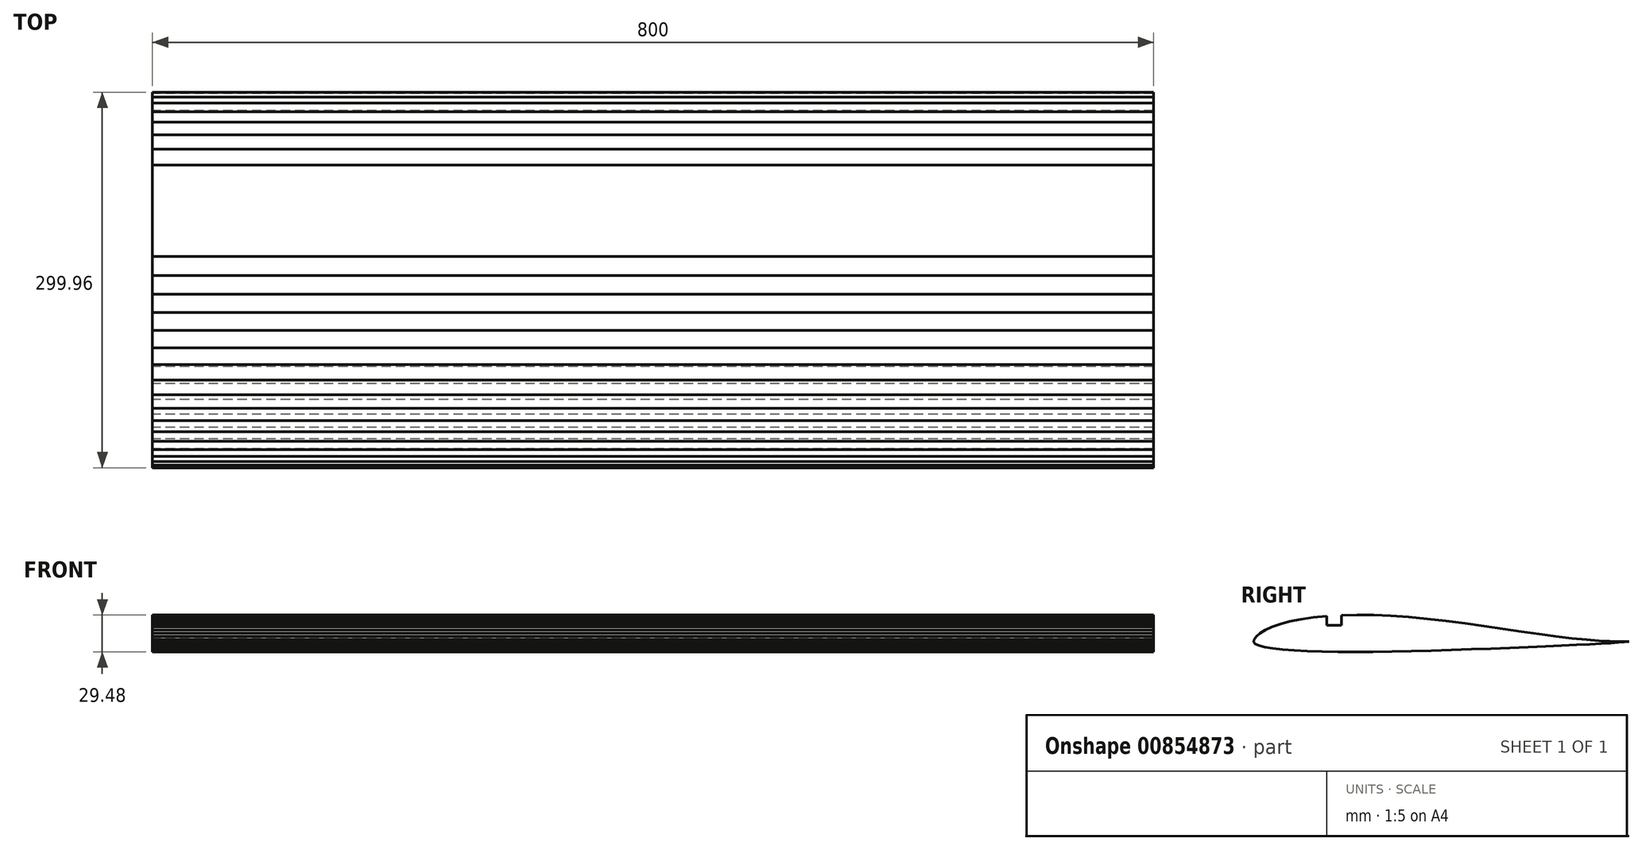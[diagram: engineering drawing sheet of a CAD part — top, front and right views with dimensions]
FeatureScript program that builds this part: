
annotation { "Feature Type Name" : "Feature", "Feature Type Description" : "" }
export const myFeature = defineFeature(function(context is Context, id is Id, definition is map)
    precondition{}
    {
        {
            var Q0;
            Q0=qCreatedBy(makeId("Right.planeOp"),FACE);
            var sketch = newSketch(context, id + "F0", { "sketchPlane" : qUnion([Q0])});
            skLineSegment(sketch, "E0", {"start": v(149.98, -6.6) * mm, "end": v(149, -6.6) * mm});
            skLineSegment(sketch, "E1", {"start": v(149, -6.6) * mm, "end": v(146.1, -6.58) * mm});
            skLineSegment(sketch, "E2", {"start": v(146.1, -6.58) * mm, "end": v(141.28, -6.49) * mm});
            skLineSegment(sketch, "E3", {"start": v(141.28, -6.49) * mm, "end": v(134.59, -6.27) * mm});
            skLineSegment(sketch, "E4", {"start": v(134.59, -6.27) * mm, "end": v(126.1, -5.83) * mm});
            skLineSegment(sketch, "E5", {"start": v(126.1, -5.83) * mm, "end": v(115.98, -5.05) * mm});
            skLineSegment(sketch, "E6", {"start": v(115.98, -5.05) * mm, "end": v(104.46, -3.89) * mm});
            skLineSegment(sketch, "E7", {"start": v(104.46, -3.89) * mm, "end": v(91.8, -2.38) * mm});
            skLineSegment(sketch, "E8", {"start": v(91.8, -2.38) * mm, "end": v(78.2, -0.57) * mm});
            skLineSegment(sketch, "E9", {"start": v(78.2, -0.57) * mm, "end": v(63.9, 1.47) * mm});
            skLineSegment(sketch, "E10", {"start": v(63.9, 1.47) * mm, "end": v(49.1, 3.66) * mm});
            skLineSegment(sketch, "E11", {"start": v(49.1, 3.66) * mm, "end": v(34.04, 5.9) * mm});
            skLineSegment(sketch, "E12", {"start": v(34.04, 5.9) * mm, "end": v(18.87, 8.03) * mm});
            skLineSegment(sketch, "E13", {"start": v(18.87, 8.03) * mm, "end": v(3.72, 9.99) * mm});
            skLineSegment(sketch, "E14", {"start": v(3.72, 9.99) * mm, "end": v(-11.27, 11.68) * mm});
            skLineSegment(sketch, "E15", {"start": v(-11.27, 11.68) * mm, "end": v(-25.98, 13.04) * mm});
            skLineSegment(sketch, "E16", {"start": v(-25.98, 13.04) * mm, "end": v(-40.3, 14.02) * mm});
            skLineSegment(sketch, "E17", {"start": v(-40.3, 14.02) * mm, "end": v(-54.12, 14.6) * mm});
            skLineSegment(sketch, "E18", {"start": v(-54.12, 14.6) * mm, "end": v(-67.34, 14.74) * mm});
            skLineSegment(sketch, "E19", {"start": v(-67.34, 14.74) * mm, "end": v(-79.87, 14.47) * mm});
            skLineSegment(sketch, "E20", {"start": v(-79.87, 14.47) * mm, "end": v(-91.6, 13.8) * mm});
            skLineSegment(sketch, "E21", {"start": v(-91.6, 13.8) * mm, "end": v(-102.44, 12.74) * mm});
            skLineSegment(sketch, "E22", {"start": v(-102.44, 12.74) * mm, "end": v(-112.3, 11.3) * mm});
            skLineSegment(sketch, "E23", {"start": v(-112.3, 11.3) * mm, "end": v(-121.11, 9.53) * mm});
            skLineSegment(sketch, "E24", {"start": v(-121.11, 9.53) * mm, "end": v(-128.8, 7.47) * mm});
            skLineSegment(sketch, "E25", {"start": v(-128.8, 7.47) * mm, "end": v(-135.36, 5.15) * mm});
            skLineSegment(sketch, "E26", {"start": v(-135.36, 5.15) * mm, "end": v(-140.72, 2.65) * mm});
            skLineSegment(sketch, "E27", {"start": v(-140.72, 2.65) * mm, "end": v(-144.87, 0.04) * mm});
            skLineSegment(sketch, "E28", {"start": v(-144.87, 0.04) * mm, "end": v(-147.8, -2.55) * mm});
            skLineSegment(sketch, "E29", {"start": v(-147.8, -2.55) * mm, "end": v(-149.52, -5) * mm});
            skLineSegment(sketch, "E30", {"start": v(-149.52, -5) * mm, "end": v(-149.98, -7.02) * mm});
            skLineSegment(sketch, "E31", {"start": v(-149.98, -7.02) * mm, "end": v(-148.75, -8.55) * mm});
            skLineSegment(sketch, "E32", {"start": v(-148.75, -8.55) * mm, "end": v(-145.65, -9.85) * mm});
            skLineSegment(sketch, "E33", {"start": v(-145.65, -9.85) * mm, "end": v(-140.94, -11.01) * mm});
            skLineSegment(sketch, "E34", {"start": v(-140.94, -11.01) * mm, "end": v(-134.65, -12) * mm});
            skLineSegment(sketch, "E35", {"start": v(-134.65, -12) * mm, "end": v(-126.87, -12.84) * mm});
            skLineSegment(sketch, "E36", {"start": v(-126.87, -12.84) * mm, "end": v(-117.67, -13.52) * mm});
            skLineSegment(sketch, "E37", {"start": v(-117.67, -13.52) * mm, "end": v(-107.15, -14.04) * mm});
            skLineSegment(sketch, "E38", {"start": v(-107.15, -14.04) * mm, "end": v(-95.44, -14.42) * mm});
            skLineSegment(sketch, "E39", {"start": v(-95.44, -14.42) * mm, "end": v(-82.68, -14.66) * mm});
            skLineSegment(sketch, "E40", {"start": v(-82.68, -14.66) * mm, "end": v(-69, -14.74) * mm});
            skLineSegment(sketch, "E41", {"start": v(-69, -14.74) * mm, "end": v(-54.54, -14.67) * mm});
            skLineSegment(sketch, "E42", {"start": v(-54.54, -14.67) * mm, "end": v(-39.43, -14.47) * mm});
            skLineSegment(sketch, "E43", {"start": v(-39.43, -14.47) * mm, "end": v(-23.86, -14.15) * mm});
            skLineSegment(sketch, "E44", {"start": v(-23.86, -14.15) * mm, "end": v(-7.99, -13.74) * mm});
            skLineSegment(sketch, "E45", {"start": v(-7.99, -13.74) * mm, "end": v(8, -13.25) * mm});
            skLineSegment(sketch, "E46", {"start": v(8, -13.25) * mm, "end": v(23.93, -12.71) * mm});
            skLineSegment(sketch, "E47", {"start": v(23.93, -12.71) * mm, "end": v(39.6, -12.14) * mm});
            skLineSegment(sketch, "E48", {"start": v(39.6, -12.14) * mm, "end": v(54.85, -11.53) * mm});
            skLineSegment(sketch, "E49", {"start": v(54.85, -11.53) * mm, "end": v(69.5, -10.93) * mm});
            skLineSegment(sketch, "E50", {"start": v(69.5, -10.93) * mm, "end": v(83.35, -10.33) * mm});
            skLineSegment(sketch, "E51", {"start": v(83.35, -10.33) * mm, "end": v(96.26, -9.74) * mm});
            skLineSegment(sketch, "E52", {"start": v(96.26, -9.74) * mm, "end": v(108.07, -9.2) * mm});
            skLineSegment(sketch, "E53", {"start": v(108.07, -9.2) * mm, "end": v(118.62, -8.67) * mm});
            skLineSegment(sketch, "E54", {"start": v(118.62, -8.67) * mm, "end": v(127.79, -8.18) * mm});
            skLineSegment(sketch, "E55", {"start": v(127.79, -8.18) * mm, "end": v(135.47, -7.7) * mm});
            skLineSegment(sketch, "E56", {"start": v(135.47, -7.7) * mm, "end": v(141.61, -7.23) * mm});
            skLineSegment(sketch, "E57", {"start": v(141.61, -7.23) * mm, "end": v(146.17, -6.86) * mm});
            skLineSegment(sketch, "E58", {"start": v(146.17, -6.86) * mm, "end": v(149.01, -6.65) * mm});
            skLineSegment(sketch, "E59", {"start": v(149.01, -6.65) * mm, "end": v(149.98, -6.6) * mm});
            skSolve(sketch);
        }
        {
            var Q0;
            Q0=makeQuery(id+"F0.imprint","IMPRINT",FACE,{"disambiguationData":[TD([[makeQuery(id+"F0.imprint","IMPRINT",EDGE,{"derivedFrom":sQuery(id+"F0.wireOp",EDGE,"E0")}),1.0]])]});
            extrude(context, id + "F1", {"entities" : qUnion([Q0]), "depth" : 800 * mm, "offsetDistance" : 25 * mm});
        }
        {
            var Q0;
            Q0=makeQuery(id+"F1.opExtrude","CAP_FACE",FACE,{"disambiguationData":[OSD([sQuery(id+"F0.wireOp",EDGE,"E0"),sQuery(id+"F0.wireOp",EDGE,"E1"),sQuery(id+"F0.wireOp",EDGE,"E2"),sQuery(id+"F0.wireOp",EDGE,"E3"),sQuery(id+"F0.wireOp",EDGE,"E4"),sQuery(id+"F0.wireOp",EDGE,"E5"),sQuery(id+"F0.wireOp",EDGE,"E6"),sQuery(id+"F0.wireOp",EDGE,"E7"),sQuery(id+"F0.wireOp",EDGE,"E8"),sQuery(id+"F0.wireOp",EDGE,"E9"),sQuery(id+"F0.wireOp",EDGE,"E10"),sQuery(id+"F0.wireOp",EDGE,"E11"),sQuery(id+"F0.wireOp",EDGE,"E12"),sQuery(id+"F0.wireOp",EDGE,"E13"),sQuery(id+"F0.wireOp",EDGE,"E14"),sQuery(id+"F0.wireOp",EDGE,"E15"),sQuery(id+"F0.wireOp",EDGE,"E16"),sQuery(id+"F0.wireOp",EDGE,"E17"),sQuery(id+"F0.wireOp",EDGE,"E18"),sQuery(id+"F0.wireOp",EDGE,"E19"),sQuery(id+"F0.wireOp",EDGE,"E20"),sQuery(id+"F0.wireOp",EDGE,"E21"),sQuery(id+"F0.wireOp",EDGE,"E22"),sQuery(id+"F0.wireOp",EDGE,"E23"),sQuery(id+"F0.wireOp",EDGE,"E24"),sQuery(id+"F0.wireOp",EDGE,"E25"),sQuery(id+"F0.wireOp",EDGE,"E26"),sQuery(id+"F0.wireOp",EDGE,"E27"),sQuery(id+"F0.wireOp",EDGE,"E28"),sQuery(id+"F0.wireOp",EDGE,"E29"),sQuery(id+"F0.wireOp",EDGE,"E30"),sQuery(id+"F0.wireOp",EDGE,"E31"),sQuery(id+"F0.wireOp",EDGE,"E32"),sQuery(id+"F0.wireOp",EDGE,"E33"),sQuery(id+"F0.wireOp",EDGE,"E34"),sQuery(id+"F0.wireOp",EDGE,"E35"),sQuery(id+"F0.wireOp",EDGE,"E36"),sQuery(id+"F0.wireOp",EDGE,"E37"),sQuery(id+"F0.wireOp",EDGE,"E38"),sQuery(id+"F0.wireOp",EDGE,"E39"),sQuery(id+"F0.wireOp",EDGE,"E40"),sQuery(id+"F0.wireOp",EDGE,"E41"),sQuery(id+"F0.wireOp",EDGE,"E42"),sQuery(id+"F0.wireOp",EDGE,"E43"),sQuery(id+"F0.wireOp",EDGE,"E44"),sQuery(id+"F0.wireOp",EDGE,"E45"),sQuery(id+"F0.wireOp",EDGE,"E46"),sQuery(id+"F0.wireOp",EDGE,"E47"),sQuery(id+"F0.wireOp",EDGE,"E48"),sQuery(id+"F0.wireOp",EDGE,"E49"),sQuery(id+"F0.wireOp",EDGE,"E50"),sQuery(id+"F0.wireOp",EDGE,"E51"),sQuery(id+"F0.wireOp",EDGE,"E52"),sQuery(id+"F0.wireOp",EDGE,"E53"),sQuery(id+"F0.wireOp",EDGE,"E54"),sQuery(id+"F0.wireOp",EDGE,"E55"),sQuery(id+"F0.wireOp",EDGE,"E56"),sQuery(id+"F0.wireOp",EDGE,"E57"),sQuery(id+"F0.wireOp",EDGE,"E58"),sQuery(id+"F0.wireOp",EDGE,"E59")])],"isStart":false});
            var sketch = newSketch(context, id + "F2", { "sketchPlane" : qUnion([Q0])});
            skLineSegment(sketch, "E60.0.0", {"start": v(146.17, -6.86) * mm, "end": v(149.01, -6.65) * mm, "construction": true});
            skLineSegment(sketch, "E60.0.1", {"start": v(149.01, -6.65) * mm, "end": v(149.98, -6.6) * mm, "construction": true});
            skLineSegment(sketch, "E60.0.2", {"start": v(149.98, -6.6) * mm, "end": v(149, -6.6) * mm, "construction": true});
            skLineSegment(sketch, "E60.0.3", {"start": v(149, -6.6) * mm, "end": v(146.1, -6.58) * mm, "construction": true});
            skLineSegment(sketch, "E60.0.4", {"start": v(146.1, -6.58) * mm, "end": v(141.28, -6.49) * mm, "construction": true});
            skLineSegment(sketch, "E60.0.5", {"start": v(141.28, -6.49) * mm, "end": v(134.59, -6.27) * mm, "construction": true});
            skLineSegment(sketch, "E60.0.6", {"start": v(134.59, -6.27) * mm, "end": v(126.1, -5.83) * mm, "construction": true});
            skLineSegment(sketch, "E60.0.7", {"start": v(126.1, -5.83) * mm, "end": v(115.98, -5.05) * mm, "construction": true});
            skLineSegment(sketch, "E60.0.8", {"start": v(115.98, -5.05) * mm, "end": v(104.46, -3.89) * mm, "construction": true});
            skLineSegment(sketch, "E60.0.9", {"start": v(104.46, -3.89) * mm, "end": v(91.8, -2.38) * mm, "construction": true});
            skLineSegment(sketch, "E60.0.10", {"start": v(91.8, -2.38) * mm, "end": v(78.2, -0.57) * mm, "construction": true});
            skLineSegment(sketch, "E60.0.11", {"start": v(78.2, -0.57) * mm, "end": v(63.9, 1.47) * mm, "construction": true});
            skLineSegment(sketch, "E60.0.12", {"start": v(63.9, 1.47) * mm, "end": v(49.1, 3.66) * mm, "construction": true});
            skLineSegment(sketch, "E60.0.13", {"start": v(49.1, 3.66) * mm, "end": v(34.04, 5.9) * mm, "construction": true});
            skLineSegment(sketch, "E60.0.14", {"start": v(34.04, 5.9) * mm, "end": v(18.87, 8.03) * mm, "construction": true});
            skLineSegment(sketch, "E60.0.15", {"start": v(18.87, 8.03) * mm, "end": v(3.72, 10) * mm, "construction": true});
            skLineSegment(sketch, "E60.0.16", {"start": v(3.72, 9.99) * mm, "end": v(-11.27, 11.68) * mm, "construction": true});
            skLineSegment(sketch, "E60.0.17", {"start": v(-11.27, 11.68) * mm, "end": v(-25.98, 13.04) * mm, "construction": true});
            skLineSegment(sketch, "E60.0.18", {"start": v(-25.98, 13.04) * mm, "end": v(-40.3, 14.02) * mm, "construction": true});
            skLineSegment(sketch, "E60.0.19", {"start": v(-40.3, 14.02) * mm, "end": v(-54.12, 14.6) * mm, "construction": true});
            skLineSegment(sketch, "E60.0.20", {"start": v(-54.12, 14.6) * mm, "end": v(-67.34, 14.74) * mm, "construction": true});
            skLineSegment(sketch, "E60.0.21", {"start": v(-67.34, 14.74) * mm, "end": v(-79.87, 14.47) * mm, "construction": true});
            skLineSegment(sketch, "E60.0.22", {"start": v(-79.87, 14.47) * mm, "end": v(-91.6, 13.8) * mm, "construction": true});
            skLineSegment(sketch, "E60.0.23", {"start": v(-91.6, 13.8) * mm, "end": v(-102.44, 12.74) * mm, "construction": true});
            skLineSegment(sketch, "E60.0.24", {"start": v(-102.44, 12.74) * mm, "end": v(-112.3, 11.3) * mm, "construction": true});
            skLineSegment(sketch, "E60.0.25", {"start": v(-112.3, 11.3) * mm, "end": v(-121.11, 9.53) * mm, "construction": true});
            skLineSegment(sketch, "E60.0.26", {"start": v(-121.11, 9.53) * mm, "end": v(-128.8, 7.47) * mm, "construction": true});
            skLineSegment(sketch, "E60.0.27", {"start": v(-128.8, 7.47) * mm, "end": v(-135.36, 5.15) * mm, "construction": true});
            skLineSegment(sketch, "E60.0.28", {"start": v(-135.36, 5.15) * mm, "end": v(-140.72, 2.65) * mm, "construction": true});
            skLineSegment(sketch, "E60.0.29", {"start": v(-140.72, 2.65) * mm, "end": v(-144.87, 0.04) * mm, "construction": true});
            skLineSegment(sketch, "E60.0.30", {"start": v(-144.87, 0.04) * mm, "end": v(-147.8, -2.55) * mm, "construction": true});
            skLineSegment(sketch, "E60.0.31", {"start": v(-147.8, -2.55) * mm, "end": v(-149.52, -5) * mm, "construction": true});
            skLineSegment(sketch, "E60.0.32", {"start": v(-149.52, -5) * mm, "end": v(-149.98, -7.02) * mm, "construction": true});
            skLineSegment(sketch, "E60.0.33", {"start": v(-149.98, -7.02) * mm, "end": v(-148.75, -8.55) * mm, "construction": true});
            skLineSegment(sketch, "E60.0.34", {"start": v(-148.75, -8.55) * mm, "end": v(-145.65, -9.85) * mm, "construction": true});
            skLineSegment(sketch, "E60.0.35", {"start": v(-145.65, -9.85) * mm, "end": v(-140.94, -11.01) * mm, "construction": true});
            skLineSegment(sketch, "E60.0.36", {"start": v(-140.94, -11.01) * mm, "end": v(-134.65, -12) * mm, "construction": true});
            skLineSegment(sketch, "E60.0.37", {"start": v(-134.65, -12) * mm, "end": v(-126.87, -12.84) * mm, "construction": true});
            skLineSegment(sketch, "E60.0.38", {"start": v(-126.87, -12.84) * mm, "end": v(-117.67, -13.52) * mm, "construction": true});
            skLineSegment(sketch, "E60.0.39", {"start": v(-117.67, -13.52) * mm, "end": v(-107.15, -14.04) * mm, "construction": true});
            skLineSegment(sketch, "E60.0.40", {"start": v(-107.15, -14.04) * mm, "end": v(-95.44, -14.42) * mm, "construction": true});
            skLineSegment(sketch, "E60.0.41", {"start": v(-95.44, -14.42) * mm, "end": v(-82.68, -14.66) * mm, "construction": true});
            skLineSegment(sketch, "E60.0.42", {"start": v(-82.68, -14.66) * mm, "end": v(-69, -14.74) * mm, "construction": true});
            skLineSegment(sketch, "E60.0.43", {"start": v(-69, -14.74) * mm, "end": v(-54.54, -14.67) * mm, "construction": true});
            skLineSegment(sketch, "E60.0.44", {"start": v(-54.54, -14.67) * mm, "end": v(-39.43, -14.47) * mm, "construction": true});
            skLineSegment(sketch, "E60.0.45", {"start": v(-39.43, -14.47) * mm, "end": v(-23.86, -14.15) * mm, "construction": true});
            skLineSegment(sketch, "E60.0.46", {"start": v(-23.86, -14.15) * mm, "end": v(-7.99, -13.74) * mm, "construction": true});
            skLineSegment(sketch, "E60.0.47", {"start": v(-7.99, -13.74) * mm, "end": v(8, -13.25) * mm, "construction": true});
            skLineSegment(sketch, "E60.0.48", {"start": v(8, -13.25) * mm, "end": v(23.93, -12.71) * mm, "construction": true});
            skLineSegment(sketch, "E60.0.49", {"start": v(23.93, -12.71) * mm, "end": v(39.6, -12.14) * mm, "construction": true});
            skLineSegment(sketch, "E60.0.50", {"start": v(39.6, -12.14) * mm, "end": v(54.85, -11.53) * mm, "construction": true});
            skLineSegment(sketch, "E60.0.51", {"start": v(54.85, -11.53) * mm, "end": v(69.5, -10.93) * mm, "construction": true});
            skLineSegment(sketch, "E60.0.52", {"start": v(69.5, -10.93) * mm, "end": v(83.35, -10.33) * mm, "construction": true});
            skLineSegment(sketch, "E60.0.53", {"start": v(83.35, -10.33) * mm, "end": v(96.26, -9.74) * mm, "construction": true});
            skLineSegment(sketch, "E60.0.54", {"start": v(96.26, -9.74) * mm, "end": v(108.07, -9.2) * mm, "construction": true});
            skLineSegment(sketch, "E60.0.55", {"start": v(108.07, -9.2) * mm, "end": v(118.62, -8.67) * mm, "construction": true});
            skLineSegment(sketch, "E60.0.56", {"start": v(118.62, -8.67) * mm, "end": v(127.79, -8.18) * mm, "construction": true});
            skLineSegment(sketch, "E60.0.57", {"start": v(127.79, -8.18) * mm, "end": v(135.47, -7.7) * mm, "construction": true});
            skLineSegment(sketch, "E60.0.58", {"start": v(135.47, -7.7) * mm, "end": v(141.61, -7.23) * mm, "construction": true});
            skLineSegment(sketch, "E60.0.59", {"start": v(141.61, -7.23) * mm, "end": v(146.17, -6.86) * mm, "construction": true});
            skLineSegment(sketch, "E61.bottom", {"start": v(-91.6, 23.1) * mm, "end": v(-79.87, 23.1) * mm});
            skLineSegment(sketch, "E61.top", {"start": v(-91.6, 6.56) * mm, "end": v(-79.87, 6.56) * mm});
            skLineSegment(sketch, "E61.left", {"start": v(-91.6, 23.1) * mm, "end": v(-91.6, 6.56) * mm});
            skLineSegment(sketch, "E61.right", {"start": v(-79.87, 23.1) * mm, "end": v(-79.87, 6.56) * mm});
            skSolve(sketch);
        }
        {
            var Q0;
            {var subQ0=sQuery(id+"F2.wireOp",EDGE,"E61.top");Q0=makeQuery(id+"F2.imprint","IMPRINT",FACE,{"disambiguationData":[TD([[makeQuery(id+"F2.imprint","IMPRINT",EDGE,{"derivedFrom":subQ0}),1.0]])]});}
            extrude(context, id + "F3", {"entities" : qUnion([Q0]), "operationType" : NewBodyOperationType.REMOVE, "endBound" : BoundingType.THROUGH_ALL, "oppositeDirection" : true, "depth" : 25 * mm, "offsetDistance" : 25 * mm});
        }
    });
